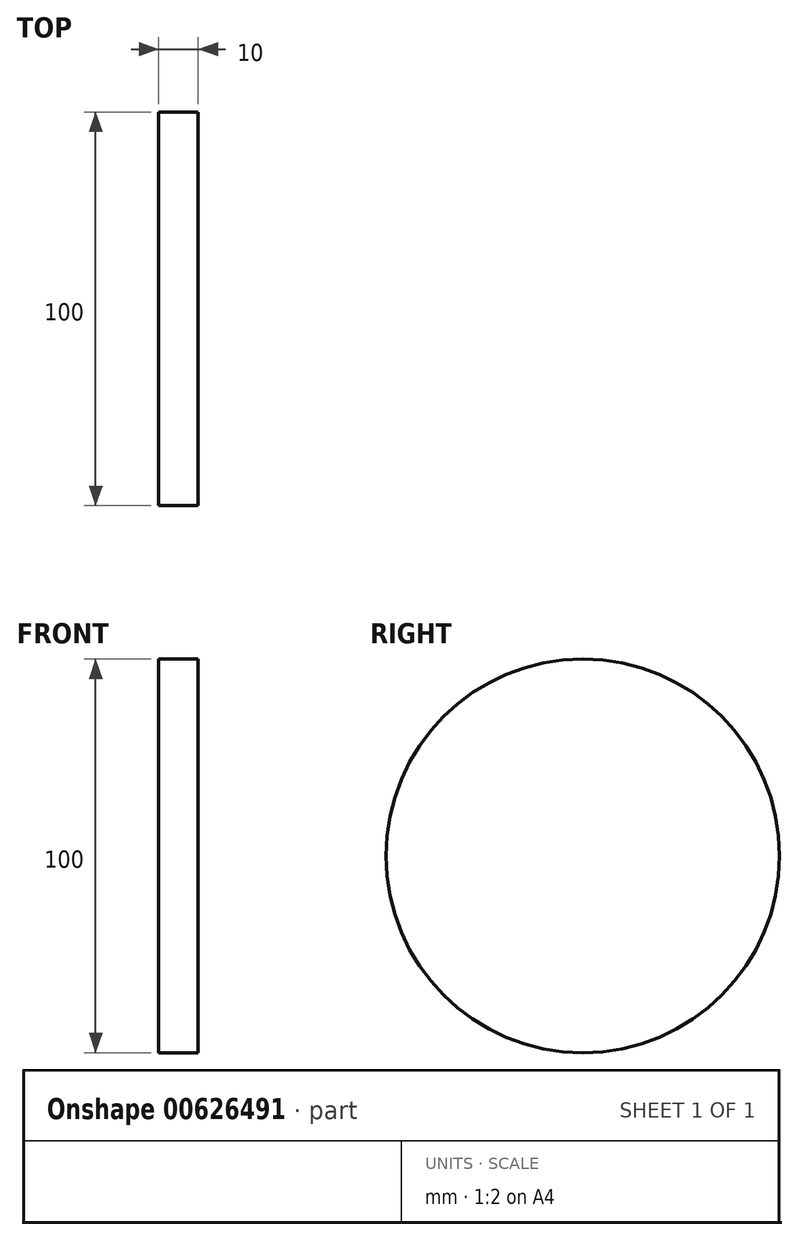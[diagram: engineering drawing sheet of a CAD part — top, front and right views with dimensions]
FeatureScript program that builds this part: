
annotation { "Feature Type Name" : "Feature", "Feature Type Description" : "" }
export const myFeature = defineFeature(function(context is Context, id is Id, definition is map)
    precondition{}
    {
        {
            var Q0;
            Q0=qCreatedBy(makeId("Right.planeOp"),FACE);
            var sketch = newSketch(context, id + "F0", { "sketchPlane" : qUnion([Q0])});
            skCircle(sketch, "E0", {"center": v(0, 0) * mm, "radius": 50 * mm});
            skSolve(sketch);
        }
        {
            var Q0;
            Q0 = qSketchRegion(id + "F0", true);
            var Q1;
            Q1=makeQuery(id+"F0.imprint","IMPRINT",FACE,{"disambiguationData":[TD([[makeQuery(id+"F0.imprint","IMPRINT",EDGE,{"derivedFrom":sQuery(id+"F0.wireOp",EDGE,"E0")}),1.0]])]});
            extrude(context, id + "F1", {"entities" : qUnion([Q0, Q1]), "endBound" : BoundingType.SYMMETRIC, "depth" : 10 * mm, "offsetDistance" : 25 * mm});
        }
    });
